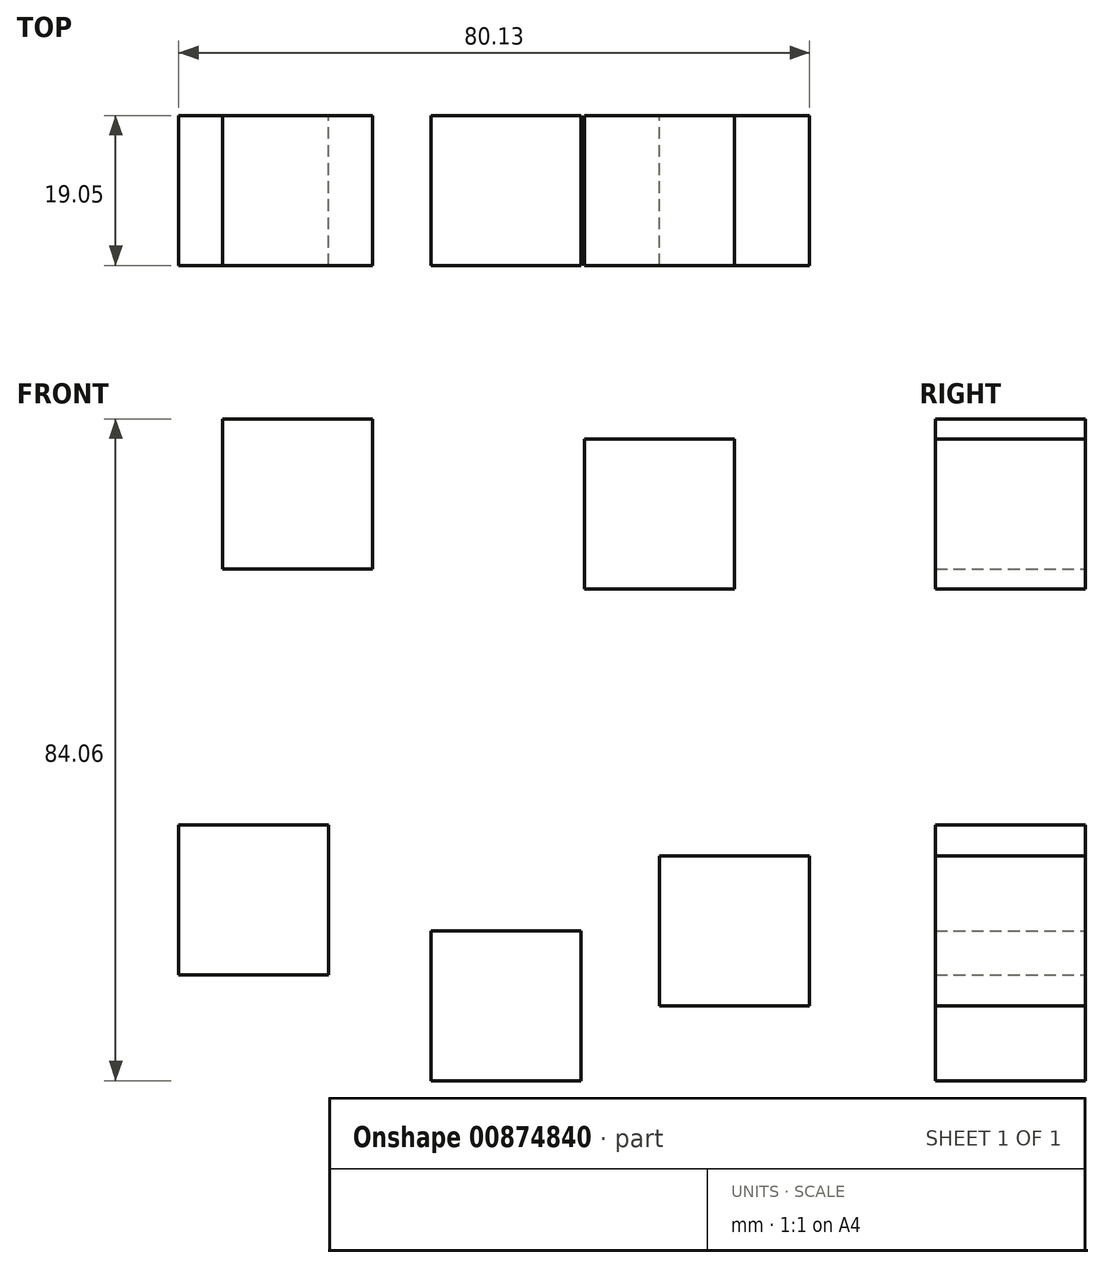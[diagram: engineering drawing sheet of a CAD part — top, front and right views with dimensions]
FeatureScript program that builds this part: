
annotation { "Feature Type Name" : "Feature", "Feature Type Description" : "" }
export const myFeature = defineFeature(function(context is Context, id is Id, definition is map)
    precondition{}
    {
        {
            var Q0;
            Q0=qCreatedBy(makeId("Front.planeOp"),FACE);
            var sketch = newSketch(context, id + "F0", { "sketchPlane" : qUnion([Q0])});
            skLineSegment(sketch, "E0.bottom", {"start": v(-26.46, 27.21) * mm, "end": v(-45.5, 27.21) * mm});
            skLineSegment(sketch, "E0.top", {"start": v(-26.46, 46.26) * mm, "end": v(-45.5, 46.26) * mm});
            skLineSegment(sketch, "E0.left", {"start": v(-26.46, 27.21) * mm, "end": v(-26.46, 46.26) * mm});
            skLineSegment(sketch, "E0.right", {"start": v(-45.5, 27.21) * mm, "end": v(-45.5, 46.26) * mm});
            skPoint(sketch, "E0.middle", {"position": v(-35.98, 36.74) * mm});
            skLineSegment(sketch, "E1.bottom", {"start": v(19.5, 24.64) * mm, "end": v(0.45, 24.64) * mm});
            skLineSegment(sketch, "E1.top", {"start": v(19.5, 43.7) * mm, "end": v(0.45, 43.7) * mm});
            skLineSegment(sketch, "E1.left", {"start": v(19.5, 24.64) * mm, "end": v(19.5, 43.7) * mm});
            skLineSegment(sketch, "E1.right", {"start": v(0.45, 24.64) * mm, "end": v(0.45, 43.7) * mm});
            skPoint(sketch, "E1.middle", {"position": v(9.98, 34.17) * mm});
            skLineSegment(sketch, "E2.bottom", {"start": v(-32.05, -24.34) * mm, "end": v(-51.1, -24.34) * mm});
            skLineSegment(sketch, "E2.top", {"start": v(-32.05, -5.3) * mm, "end": v(-51.1, -5.3) * mm});
            skLineSegment(sketch, "E2.left", {"start": v(-32.05, -24.34) * mm, "end": v(-32.05, -5.3) * mm});
            skLineSegment(sketch, "E2.right", {"start": v(-51.1, -24.34) * mm, "end": v(-51.1, -5.3) * mm});
            skPoint(sketch, "E2.middle", {"position": v(-41.58, -14.82) * mm});
            skLineSegment(sketch, "E3.bottom", {"start": v(29.03, -28.27) * mm, "end": v(9.98, -28.27) * mm});
            skLineSegment(sketch, "E3.top", {"start": v(29.03, -9.22) * mm, "end": v(9.98, -9.22) * mm});
            skLineSegment(sketch, "E3.left", {"start": v(29.03, -28.27) * mm, "end": v(29.03, -9.22) * mm});
            skLineSegment(sketch, "E3.right", {"start": v(9.98, -28.27) * mm, "end": v(9.98, -9.22) * mm});
            skPoint(sketch, "E3.middle", {"position": v(19.5, -18.75) * mm});
            skLineSegment(sketch, "E4.bottom", {"start": v(0, -37.8) * mm, "end": v(-19.05, -37.8) * mm});
            skLineSegment(sketch, "E4.top", {"start": v(0, -18.75) * mm, "end": v(-19.05, -18.75) * mm});
            skLineSegment(sketch, "E4.left", {"start": v(0, -37.8) * mm, "end": v(0, -18.75) * mm});
            skLineSegment(sketch, "E4.right", {"start": v(-19.05, -37.8) * mm, "end": v(-19.05, -18.75) * mm});
            skPoint(sketch, "E4.middle", {"position": v(-9.53, -28.27) * mm});
            skSolve(sketch);
        }
        {
            var Q0;
            Q0=makeQuery(id+"F0.imprint","IMPRINT",FACE,{"disambiguationData":[TD([[makeQuery(id+"F0.imprint","IMPRINT",EDGE,{"derivedFrom":sQuery(id+"F0.wireOp",EDGE,"E0.bottom")}),-1.0]])]});
            var Q1;
            Q1=makeQuery(id+"F0.imprint","IMPRINT",FACE,{"disambiguationData":[TD([[makeQuery(id+"F0.imprint","IMPRINT",EDGE,{"derivedFrom":sQuery(id+"F0.wireOp",EDGE,"E1.bottom")}),-1.0]])]});
            var Q2;
            Q2=makeQuery(id+"F0.imprint","IMPRINT",FACE,{"disambiguationData":[TD([[makeQuery(id+"F0.imprint","IMPRINT",EDGE,{"derivedFrom":sQuery(id+"F0.wireOp",EDGE,"E2.bottom")}),-1.0]])]});
            var Q3;
            Q3=makeQuery(id+"F0.imprint","IMPRINT",FACE,{"disambiguationData":[TD([[makeQuery(id+"F0.imprint","IMPRINT",EDGE,{"derivedFrom":sQuery(id+"F0.wireOp",EDGE,"E4.bottom")}),-1.0]])]});
            var Q4;
            Q4=makeQuery(id+"F0.imprint","IMPRINT",FACE,{"disambiguationData":[TD([[makeQuery(id+"F0.imprint","IMPRINT",EDGE,{"derivedFrom":sQuery(id+"F0.wireOp",EDGE,"E3.bottom")}),-1.0]])]});
            extrude(context, id + "F1", {"entities" : qUnion([Q0, Q1, Q2, Q3, Q4]), "depth" : 19.05 * mm, "offsetDistance" : 25.4 * mm});
        }
    });
